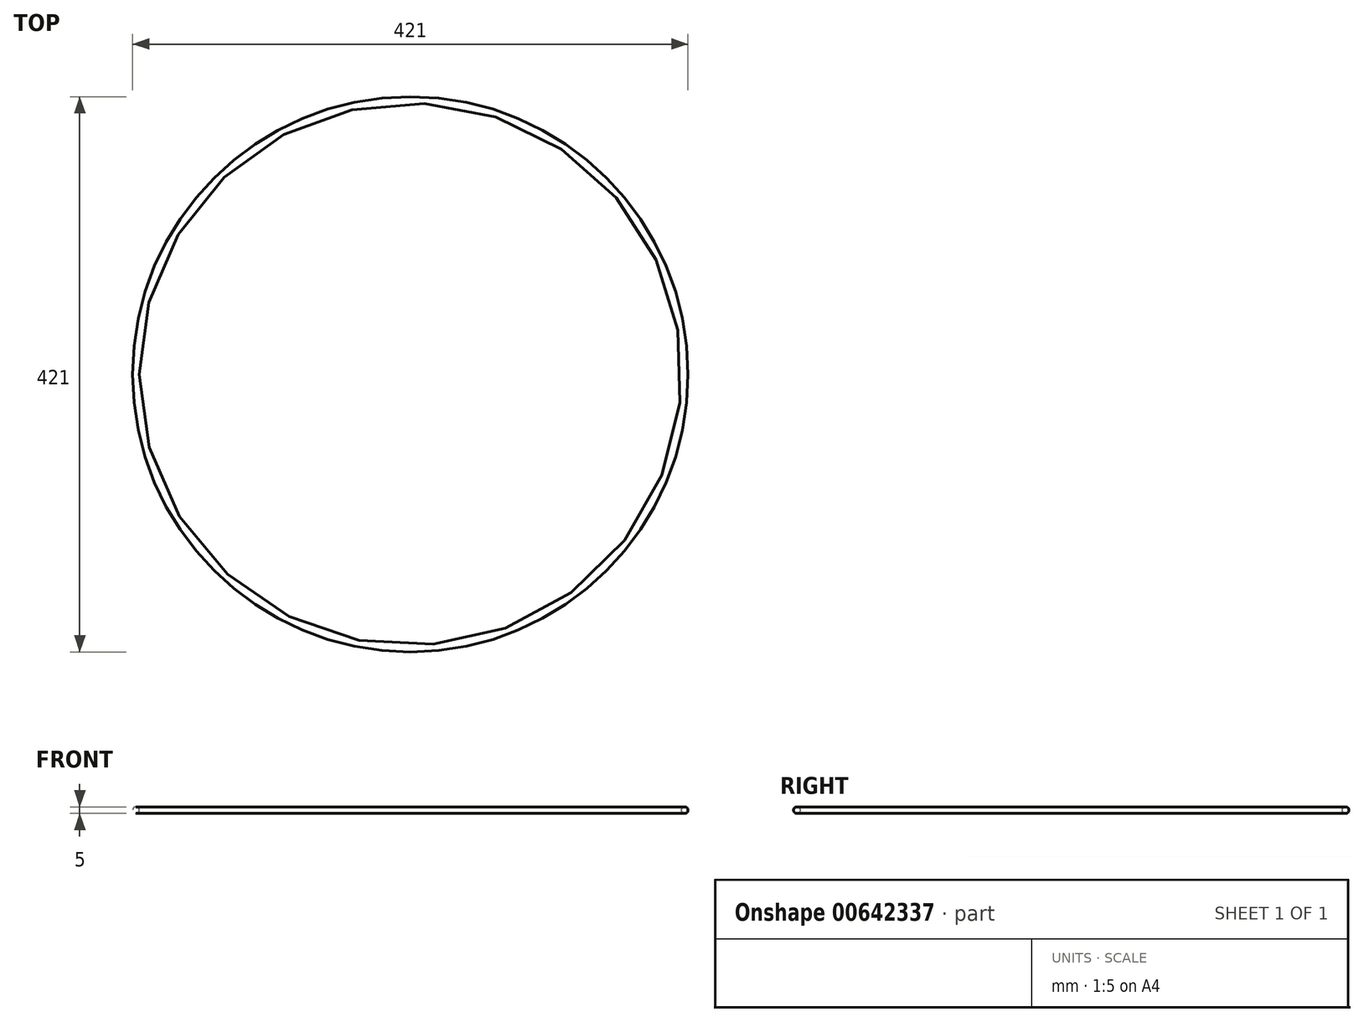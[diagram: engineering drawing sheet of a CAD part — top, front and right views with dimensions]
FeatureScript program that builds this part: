
annotation { "Feature Type Name" : "Feature", "Feature Type Description" : "" }
export const myFeature = defineFeature(function(context is Context, id is Id, definition is map)
    precondition{}
    {
        {
            var Q0;
            Q0=qCreatedBy(makeId("Front.planeOp"),FACE);
            var sketch = newSketch(context, id + "F0", { "sketchPlane" : qUnion([Q0])});
            skCircle(sketch, "E0", {"center": v(208, 0) * mm, "radius": 2.5 * mm});
            skSolve(sketch);
        }
        {
            var Q0;
            Q0=qCreatedBy(makeId("Front.planeOp"),FACE);
            var sketch = newSketch(context, id + "F1", { "sketchPlane" : qUnion([Q0])});
            skLineSegment(sketch, "E1", {"start": v(0, 0) * mm, "end": v(0, 60) * mm, "construction": true});
            skSolve(sketch);
        }
        {
            var Q0;
            Q0=makeQuery(id+"F0.imprint","IMPRINT",FACE,{"disambiguationData":[TD([[makeQuery(id+"F0.imprint","IMPRINT",EDGE,{"derivedFrom":sQuery(id+"F0.wireOp",EDGE,"E0")}),1.0]])]});
            var Q1;
            Q1=sQuery(id+"F1.wireOp",EDGE,"E1");
            revolve(context, id + "F2", {"entities" : qUnion([Q0]), "axis" : qUnion([Q1]), "revolveType" : RevolveType.FULL});
        }
    });
